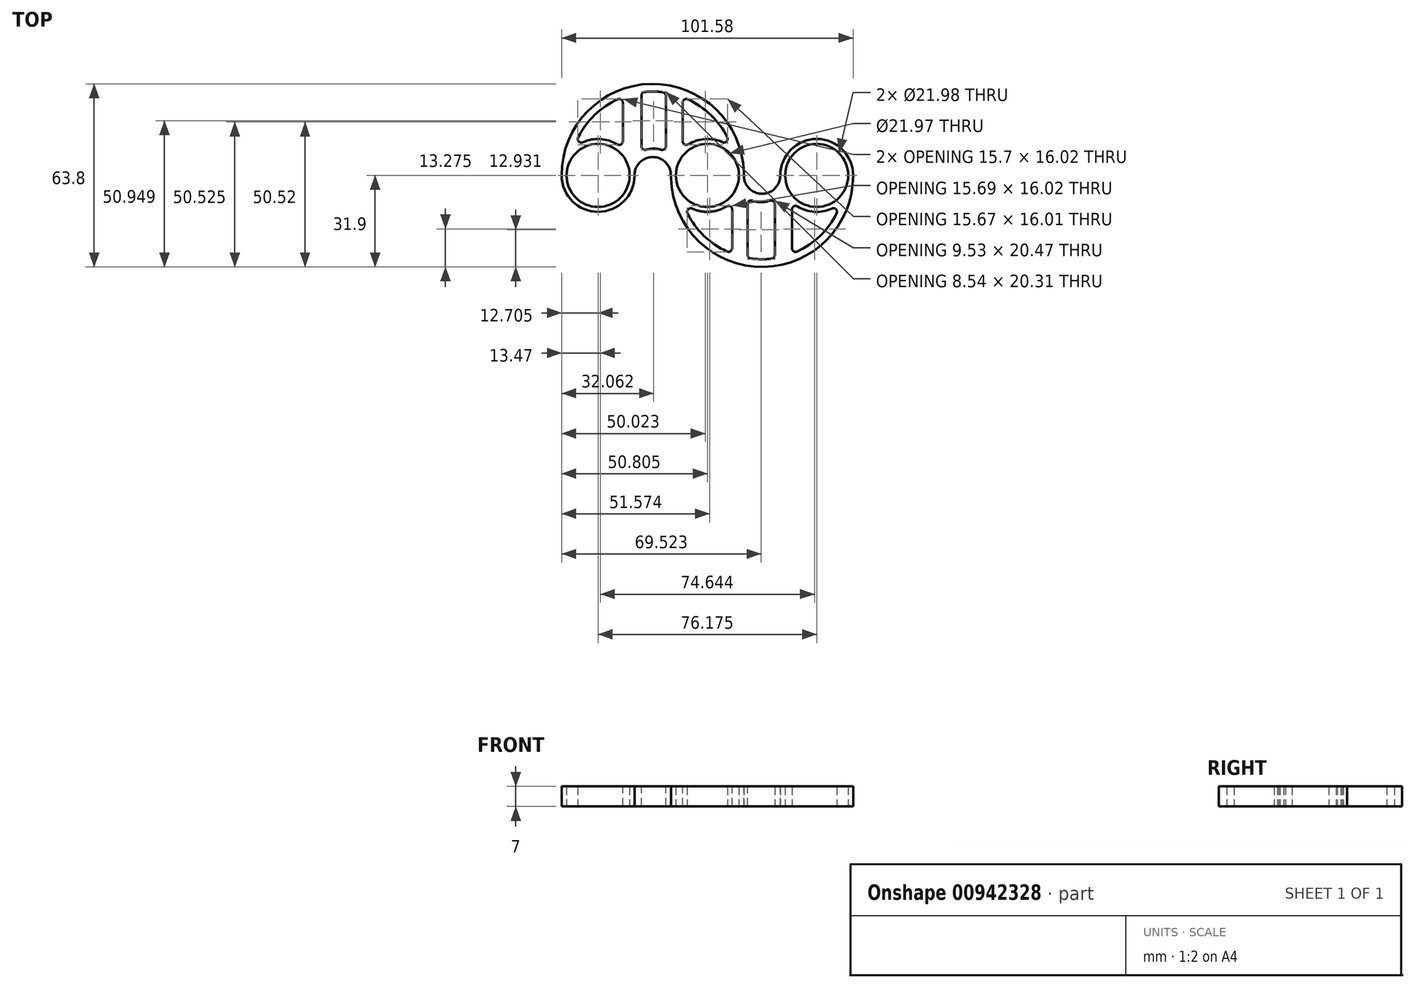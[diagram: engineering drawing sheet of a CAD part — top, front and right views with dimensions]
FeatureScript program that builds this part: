
annotation { "Feature Type Name" : "Feature", "Feature Type Description" : "" }
export const myFeature = defineFeature(function(context is Context, id is Id, definition is map)
    precondition{}
    {
        {
            var Q0;
            Q0=qCreatedBy(makeId("Top.planeOp"),FACE);
            var sketch = newSketch(context, id + "F0", { "sketchPlane" : qUnion([Q0])});
            skCircle(sketch, "E0", {"center": v(-38.08, 0) * mm, "radius": 10.99 * mm});
            skCircle(sketch, "E1", {"center": v(-38.08, 0) * mm, "radius": 12.7 * mm});
            skCircle(sketch, "E2", {"center": v(0, 0) * mm, "radius": 12.7 * mm});
            skArc(sketch, "E3", {"start": v(-12.7, 0) * mm, "mid": v(-19.04, 6.4) * mm, "end": v(-25.38, 0) * mm});
            skArc(sketch, "E4", {"start": v(-11.4, 5.59) * mm, "mid": v(-19.06, 9.33) * mm, "end": v(-26.4, 5.02) * mm});
            skArc(sketch, "E5", {"start": v(12.7, 0) * mm, "mid": v(-19.04, 31.9) * mm, "end": v(-50.78, 0) * mm});
            skArc(sketch, "E6", {"start": v(8.62, 9.33) * mm, "mid": v(-19.04, 29.2) * mm, "end": v(-46.7, 9.33) * mm});
            skPoint(sketch, "E6.startSnap0", {"position": v(-19.06, 9.33) * mm});
            skPoint(sketch, "E6.endSnap0", {"position": v(-19.06, 9.33) * mm});
            skCircle(sketch, "E7", {"center": v(0.02, 0) * mm, "radius": 10.99 * mm});
            skCircle(sketch, "E8", {"center": v(38.1, 0) * mm, "radius": 10.99 * mm});
            skCircle(sketch, "E9", {"center": v(38.1, 0) * mm, "radius": 12.7 * mm});
            skCircle(sketch, "E10", {"center": v(0.02, 0) * mm, "radius": 12.7 * mm});
            skArc(sketch, "E11", {"start": v(12.72, 0) * mm, "mid": v(19.06, -6.4) * mm, "end": v(25.4, 0) * mm});
            skArc(sketch, "E12", {"start": v(11.43, -5.59) * mm, "mid": v(19.08, -9.33) * mm, "end": v(26.43, -5.02) * mm});
            skArc(sketch, "E13", {"start": v(-12.68, 0) * mm, "mid": v(19.06, -31.9) * mm, "end": v(50.8, 0) * mm});
            skArc(sketch, "E14", {"start": v(-8.6, -9.33) * mm, "mid": v(19.06, -29.2) * mm, "end": v(46.72, -9.33) * mm});
            skPoint(sketch, "E14.startSnap0", {"position": v(19.08, -9.33) * mm});
            skPoint(sketch, "E14.endSnap0", {"position": v(19.08, -9.33) * mm});
            skLineSegment(sketch, "E15", {"start": v(29.48, -9.33) * mm, "end": v(29.48, -27.28) * mm});
            skLineSegment(sketch, "E16", {"start": v(8.64, -9.33) * mm, "end": v(8.64, -27.28) * mm});
            skLineSegment(sketch, "E17", {"start": v(-29.46, 9.33) * mm, "end": v(-29.46, 27.28) * mm});
            skLineSegment(sketch, "E18", {"start": v(-8.6, 9.33) * mm, "end": v(-8.6, 27.27) * mm});
            skLineSegment(sketch, "E19", {"start": v(-23, 8.26) * mm, "end": v(-23, 28.94) * mm});
            skLineSegment(sketch, "E20", {"start": v(-14.45, 8.26) * mm, "end": v(-14.45, 28.84) * mm});
            skLineSegment(sketch, "E21", {"start": v(23.5, -7.97) * mm, "end": v(23.5, -28.87) * mm});
            skLineSegment(sketch, "E22", {"start": v(13.98, -7.97) * mm, "end": v(13.98, -28.76) * mm});
            skSolve(sketch);
        }
        {
            var Q0;
            Q0=makeQuery(id+"F0.imprint","IMPRINT",FACE,{"disambiguationData":[TD([[makeQuery(id+"F0.imprint","IMPRINT",EDGE,{"derivedFrom":sQuery(id+"F0.wireOp",EDGE,"E7")}),-1.0]])]});
            var Q1;
            {var subQ0=sQuery(id+"F0.wireOp",EDGE,"E11");Q1=makeQuery(id+"F0.imprint","IMPRINT",FACE,{"disambiguationData":[TD([[makeQuery(id+"F0.imprint","IMPRINT",EDGE,{"derivedFrom":subQ0}),-1.0]])]});}
            var Q2;
            {var subQ0=sQuery(id+"F0.wireOp",EDGE,"E13");var subQ1=sQuery(id+"F0.wireOp",EDGE,"E2");var subQ2=makeQuery(id+"F0.imprint","INTERSECT",VERTEX,{"derivedFrom":[subQ1,subQ0]});Q2=makeQuery(id+"F0.imprint","IMPRINT",FACE,{"disambiguationData":[TD([[makeQuery(id+"F0.imprint","IMPRINT",EDGE,{"disambiguationData":[TD([[subQ2,-1.0]])],"derivedFrom":subQ1}),-1.0]])]});}
            var Q3;
            {var subQ0=sQuery(id+"F0.wireOp",EDGE,"E3");Q3=makeQuery(id+"F0.imprint","IMPRINT",FACE,{"disambiguationData":[TD([[makeQuery(id+"F0.imprint","IMPRINT",EDGE,{"derivedFrom":subQ0}),-1.0]])]});}
            var Q4;
            Q4=makeQuery(id+"F0.imprint","IMPRINT",FACE,{"disambiguationData":[TD([[makeQuery(id+"F0.imprint","IMPRINT",EDGE,{"derivedFrom":sQuery(id+"F0.wireOp",EDGE,"E0")}),-1.0]])]});
            var Q5;
            Q5=makeQuery(id+"F0.imprint","IMPRINT",FACE,{"disambiguationData":[TD([[makeQuery(id+"F0.imprint","IMPRINT",EDGE,{"derivedFrom":sQuery(id+"F0.wireOp",EDGE,"E8")}),-1.0]])]});
            var Q6;
            {var subQ0=sQuery(id+"F0.wireOp",EDGE,"E14");var subQ1=sQuery(id+"F0.wireOp",EDGE,"E2");var subQ2=makeQuery(id+"F0.imprint","INTERSECT",VERTEX,{"derivedFrom":[subQ1,subQ0]});Q6=makeQuery(id+"F0.imprint","IMPRINT",FACE,{"disambiguationData":[TD([[makeQuery(id+"F0.imprint","IMPRINT",EDGE,{"disambiguationData":[TD([[subQ2,-1.0]])],"derivedFrom":subQ1}),1.0]])]});}
            var Q7;
            {var subQ0=sQuery(id+"F0.wireOp",EDGE,"E13");var subQ1=sQuery(id+"F0.wireOp",EDGE,"E2");var subQ2=makeQuery(id+"F0.imprint","INTERSECT",VERTEX,{"derivedFrom":[subQ1,subQ0]});Q7=makeQuery(id+"F0.imprint","IMPRINT",FACE,{"disambiguationData":[TD([[makeQuery(id+"F0.imprint","IMPRINT",EDGE,{"disambiguationData":[TD([[subQ2,-1.0]])],"derivedFrom":subQ1}),1.0]])]});}
            var Q8;
            {var subQ0=sQuery(id+"F0.wireOp",EDGE,"E5");var subQ1=sQuery(id+"F0.wireOp",EDGE,"E2");var subQ2=makeQuery(id+"F0.imprint","INTERSECT",VERTEX,{"derivedFrom":[subQ1,subQ0]});Q8=makeQuery(id+"F0.imprint","IMPRINT",FACE,{"disambiguationData":[TD([[makeQuery(id+"F0.imprint","IMPRINT",EDGE,{"disambiguationData":[TD([[subQ2,-1.0]])],"derivedFrom":subQ1}),-1.0]])]});}
            var Q9;
            {var subQ0=sQuery(id+"F0.wireOp",EDGE,"E6");var subQ1=sQuery(id+"F0.wireOp",EDGE,"E2");var subQ2=makeQuery(id+"F0.imprint","INTERSECT",VERTEX,{"derivedFrom":[subQ1,subQ0]});Q9=makeQuery(id+"F0.imprint","IMPRINT",FACE,{"disambiguationData":[TD([[makeQuery(id+"F0.imprint","IMPRINT",EDGE,{"disambiguationData":[TD([[subQ2,-1.0]])],"derivedFrom":subQ1}),-1.0]])]});}
            var Q10;
            {var subQ0=sQuery(id+"F0.wireOp",EDGE,"E2");var subQ4=makeQuery(id+"F0.imprint","INTERSECT",VERTEX,{"derivedFrom":[subQ0,sQuery(id+"F0.wireOp",EDGE,"E4")]});Q10=makeQuery(id+"F0.imprint","IMPRINT",FACE,{"disambiguationData":[TD([[makeQuery(id+"F0.imprint","IMPRINT",EDGE,{"disambiguationData":[TD([[subQ4,1.0]])],"derivedFrom":subQ0}),1.0]])]});}
            var Q11;
            {var subQ3=sQuery(id+"F0.wireOp",EDGE,"E5");var subQ4=sQuery(id+"F0.wireOp",EDGE,"E2");var subQ5=makeQuery(id+"F0.imprint","INTERSECT",VERTEX,{"derivedFrom":[subQ4,subQ3]});Q11=makeQuery(id+"F0.imprint","IMPRINT",FACE,{"disambiguationData":[TD([[makeQuery(id+"F0.imprint","IMPRINT",EDGE,{"disambiguationData":[TD([[subQ5,1.0]])],"derivedFrom":subQ4}),-1.0]])]});}
            var Q12;
            {var subQ0=sQuery(id+"F0.wireOp",EDGE,"E5");var subQ1=sQuery(id+"F0.wireOp",EDGE,"E1");var subQ2=makeQuery(id+"F0.imprint","INTERSECT",VERTEX,{"derivedFrom":[subQ1,subQ0]});Q12=makeQuery(id+"F0.imprint","IMPRINT",FACE,{"disambiguationData":[TD([[makeQuery(id+"F0.imprint","IMPRINT",EDGE,{"disambiguationData":[TD([[subQ2,1.0]])],"derivedFrom":subQ1}),-1.0]])]});}
            var Q13;
            {var subQ0=sQuery(id+"F0.wireOp",EDGE,"DTZOGkMn-nSdI-sWcP-Samk-YdO5q2ABsoRK");Q13=makeQuery(id+"F0.imprint","IMPRINT",FACE,{"disambiguationData":[TD([[makeQuery(id+"F0.imprint","IMPRINT",EDGE,{"derivedFrom":subQ0}),-1.0]])]});}
            var Q14;
            {var subQ3=sQuery(id+"F0.wireOp",EDGE,"25TYoZCd-IREL-xMh5-7Hmf-XP7vreaXs02i");Q14=makeQuery(id+"F0.imprint","IMPRINT",FACE,{"disambiguationData":[TD([[makeQuery(id+"F0.imprint","IMPRINT",EDGE,{"derivedFrom":subQ3}),-1.0]])]});}
            var Q15;
            {var subQ7=sQuery(id+"F0.wireOp",EDGE,"E20");Q15=makeQuery(id+"F0.imprint","IMPRINT",FACE,{"disambiguationData":[TD([[makeQuery(id+"F0.imprint","IMPRINT",EDGE,{"derivedFrom":subQ7}),-1.0]])]});}
            var Q16;
            {var subQ0=sQuery(id+"F0.wireOp",EDGE,"E17");Q16=makeQuery(id+"F0.imprint","IMPRINT",FACE,{"disambiguationData":[TD([[makeQuery(id+"F0.imprint","IMPRINT",EDGE,{"derivedFrom":subQ0}),-1.0]])]});}
            var Q17;
            {var subQ4=sQuery(id+"F0.wireOp",EDGE,"E16");Q17=makeQuery(id+"F0.imprint","IMPRINT",FACE,{"disambiguationData":[TD([[makeQuery(id+"F0.imprint","IMPRINT",EDGE,{"derivedFrom":subQ4}),1.0]])]});}
            var Q18;
            {var subQ0=sQuery(id+"F0.wireOp",EDGE,"E15");Q18=makeQuery(id+"F0.imprint","IMPRINT",FACE,{"disambiguationData":[TD([[makeQuery(id+"F0.imprint","IMPRINT",EDGE,{"derivedFrom":subQ0}),-1.0]])]});}
            extrude(context, id + "F1", {"entities" : qUnion([Q0, Q1, Q2, Q3, Q4, Q5, Q6, Q7, Q8, Q9, Q10, Q11, Q12, Q13, Q14, Q15, Q16, Q17, Q18]), "depth" : 7 * mm, "offsetDistance" : 25.4 * mm});
        }
        {
            var Q0;
            Q0=makeQuery(id+"F1.opExtrude","SWEPT_EDGE",EDGE,{"disambiguationData":[OSD([sQuery(id+"F0.wireOp",EDGE,"E1"),sQuery(id+"F0.wireOp",EDGE,"E5")])]});
            var Q1;
            Q1=makeQuery(id+"F1.opExtrude","SWEPT_EDGE",EDGE,{"disambiguationData":[OSD([sQuery(id+"F0.wireOp",EDGE,"E2"),sQuery(id+"F0.wireOp",EDGE,"E3")])]});
            var Q2;
            Q2=makeQuery(id+"F1.opExtrude","SWEPT_EDGE",EDGE,{"disambiguationData":[OSD([sQuery(id+"F0.wireOp",EDGE,"E2"),sQuery(id+"F0.wireOp",EDGE,"E13")])]});
            var Q3;
            Q3=makeQuery(id+"F1.opExtrude","SWEPT_EDGE",EDGE,{"disambiguationData":[OSD([sQuery(id+"F0.wireOp",EDGE,"E1"),sQuery(id+"F0.wireOp",EDGE,"E3")])]});
            var Q4;
            {var subQ0=sQuery(id+"F0.wireOp",EDGE,"E10");var subQ1=sQuery(id+"F0.wireOp",EDGE,"E2");Q4=makeQuery(id+"F1.opExtrude","SWEPT_EDGE",EDGE,{"disambiguationData":[OSD([subQ1,subQ0]),TDD([makeQuery(id+"F0.imprint","INTERSECT",VERTEX,{"disambiguationData":[OD(0.0)],"derivedFrom":[subQ1,subQ0]})])]});}
            var Q5;
            Q5=makeQuery(id+"F1.opExtrude","SWEPT_EDGE",EDGE,{"disambiguationData":[OSD([sQuery(id+"F0.wireOp",EDGE,"E5"),sQuery(id+"F0.wireOp",EDGE,"E10")])]});
            var Q6;
            Q6=makeQuery(id+"F1.opExtrude","SWEPT_EDGE",EDGE,{"disambiguationData":[OSD([sQuery(id+"F0.wireOp",EDGE,"E10"),sQuery(id+"F0.wireOp",EDGE,"E11")])]});
            var Q7;
            Q7=makeQuery(id+"F1.opExtrude","SWEPT_EDGE",EDGE,{"disambiguationData":[OSD([sQuery(id+"F0.wireOp",EDGE,"E9"),sQuery(id+"F0.wireOp",EDGE,"E11")])]});
            var Q8;
            Q8=makeQuery(id+"F1.opExtrude","SWEPT_EDGE",EDGE,{"disambiguationData":[OSD([sQuery(id+"F0.wireOp",EDGE,"E9"),sQuery(id+"F0.wireOp",EDGE,"E13")])]});
            var Q9;
            {var subQ0=sQuery(id+"F0.wireOp",EDGE,"E10");var subQ1=sQuery(id+"F0.wireOp",EDGE,"E2");Q9=makeQuery(id+"F1.opExtrude","SWEPT_EDGE",EDGE,{"disambiguationData":[OSD([subQ1,subQ0]),TDD([makeQuery(id+"F0.imprint","INTERSECT",VERTEX,{"disambiguationData":[OD(1.0)],"derivedFrom":[subQ1,subQ0]})])]});}
            fillet(context, id + "F2", {"entities" : qUnion([Q0, Q1, Q2, Q3, Q4, Q5, Q6, Q7, Q8, Q9]), "radius" : 5.08 * mm, "tangentPropagation" : true, "allowEdgeOverflow" : false});
        }
        {
            var Q0;
            Q0=makeQuery(id+"F1.opExtrude","SWEPT_EDGE",EDGE,{"disambiguationData":[OSD([sQuery(id+"F0.wireOp",EDGE,"E14"),sQuery(id+"F0.wireOp",EDGE,"E15")])]});
            var Q1;
            Q1=makeQuery(id+"F1.opExtrude","SWEPT_EDGE",EDGE,{"disambiguationData":[OSD([sQuery(id+"F0.wireOp",EDGE,"E9"),sQuery(id+"F0.wireOp",EDGE,"E15")])]});
            var Q2;
            Q2=makeQuery(id+"F1.opExtrude","SWEPT_EDGE",EDGE,{"disambiguationData":[OSD([sQuery(id+"F0.wireOp",EDGE,"E9"),sQuery(id+"F0.wireOp",EDGE,"E14")])]});
            var Q3;
            Q3=makeQuery(id+"F1.opExtrude","SWEPT_EDGE",EDGE,{"disambiguationData":[OSD([sQuery(id+"F0.wireOp",EDGE,"E12"),sQuery(id+"F0.wireOp",EDGE,"E21")])]});
            var Q4;
            Q4=makeQuery(id+"F1.opExtrude","SWEPT_EDGE",EDGE,{"disambiguationData":[OSD([sQuery(id+"F0.wireOp",EDGE,"E12"),sQuery(id+"F0.wireOp",EDGE,"E22")])]});
            var Q5;
            Q5=makeQuery(id+"F1.opExtrude","SWEPT_EDGE",EDGE,{"disambiguationData":[OSD([sQuery(id+"F0.wireOp",EDGE,"E14"),sQuery(id+"F0.wireOp",EDGE,"E21")])]});
            var Q6;
            Q6=makeQuery(id+"F1.opExtrude","SWEPT_EDGE",EDGE,{"disambiguationData":[OSD([sQuery(id+"F0.wireOp",EDGE,"E14"),sQuery(id+"F0.wireOp",EDGE,"E22")])]});
            var Q7;
            Q7=makeQuery(id+"F1.opExtrude","SWEPT_EDGE",EDGE,{"disambiguationData":[OSD([sQuery(id+"F0.wireOp",EDGE,"E14"),sQuery(id+"F0.wireOp",EDGE,"E16")])]});
            var Q8;
            Q8=makeQuery(id+"F1.opExtrude","SWEPT_EDGE",EDGE,{"disambiguationData":[OSD([sQuery(id+"F0.wireOp",EDGE,"E10"),sQuery(id+"F0.wireOp",EDGE,"E16")])]});
            var Q9;
            Q9=makeQuery(id+"F1.opExtrude","SWEPT_EDGE",EDGE,{"disambiguationData":[OSD([sQuery(id+"F0.wireOp",EDGE,"E2"),sQuery(id+"F0.wireOp",EDGE,"E14")])]});
            var Q10;
            Q10=makeQuery(id+"F1.opExtrude","SWEPT_EDGE",EDGE,{"disambiguationData":[OSD([sQuery(id+"F0.wireOp",EDGE,"E6"),sQuery(id+"F0.wireOp",EDGE,"E19")])]});
            var Q11;
            Q11=makeQuery(id+"F1.opExtrude","SWEPT_EDGE",EDGE,{"disambiguationData":[OSD([sQuery(id+"F0.wireOp",EDGE,"E6"),sQuery(id+"F0.wireOp",EDGE,"E18")])]});
            var Q12;
            Q12=makeQuery(id+"F1.opExtrude","SWEPT_EDGE",EDGE,{"disambiguationData":[OSD([sQuery(id+"F0.wireOp",EDGE,"E6"),sQuery(id+"F0.wireOp",EDGE,"E10")])]});
            var Q13;
            Q13=makeQuery(id+"F1.opExtrude","SWEPT_EDGE",EDGE,{"disambiguationData":[OSD([sQuery(id+"F0.wireOp",EDGE,"E10"),sQuery(id+"F0.wireOp",EDGE,"E18")])]});
            var Q14;
            Q14=makeQuery(id+"F1.opExtrude","SWEPT_EDGE",EDGE,{"disambiguationData":[OSD([sQuery(id+"F0.wireOp",EDGE,"E4"),sQuery(id+"F0.wireOp",EDGE,"E19")])]});
            var Q15;
            Q15=makeQuery(id+"F1.opExtrude","SWEPT_EDGE",EDGE,{"disambiguationData":[OSD([sQuery(id+"F0.wireOp",EDGE,"E4"),sQuery(id+"F0.wireOp",EDGE,"E20")])]});
            var Q16;
            Q16=makeQuery(id+"F1.opExtrude","SWEPT_EDGE",EDGE,{"disambiguationData":[OSD([sQuery(id+"F0.wireOp",EDGE,"E6"),sQuery(id+"F0.wireOp",EDGE,"E20")])]});
            var Q17;
            Q17=makeQuery(id+"F1.opExtrude","SWEPT_EDGE",EDGE,{"disambiguationData":[OSD([sQuery(id+"F0.wireOp",EDGE,"E1"),sQuery(id+"F0.wireOp",EDGE,"E17")])]});
            var Q18;
            Q18=makeQuery(id+"F1.opExtrude","SWEPT_EDGE",EDGE,{"disambiguationData":[OSD([sQuery(id+"F0.wireOp",EDGE,"E6"),sQuery(id+"F0.wireOp",EDGE,"E17")])]});
            var Q19;
            Q19=makeQuery(id+"F1.opExtrude","SWEPT_EDGE",EDGE,{"disambiguationData":[OSD([sQuery(id+"F0.wireOp",EDGE,"E1"),sQuery(id+"F0.wireOp",EDGE,"E6")])]});
            fillet(context, id + "F3", {"entities" : qUnion([Q0, Q1, Q2, Q3, Q4, Q5, Q6, Q7, Q8, Q9, Q10, Q11, Q12, Q13, Q14, Q15, Q16, Q17, Q18, Q19]), "radius" : 1.27 * mm, "tangentPropagation" : true, "allowEdgeOverflow" : false});
        }
    });
